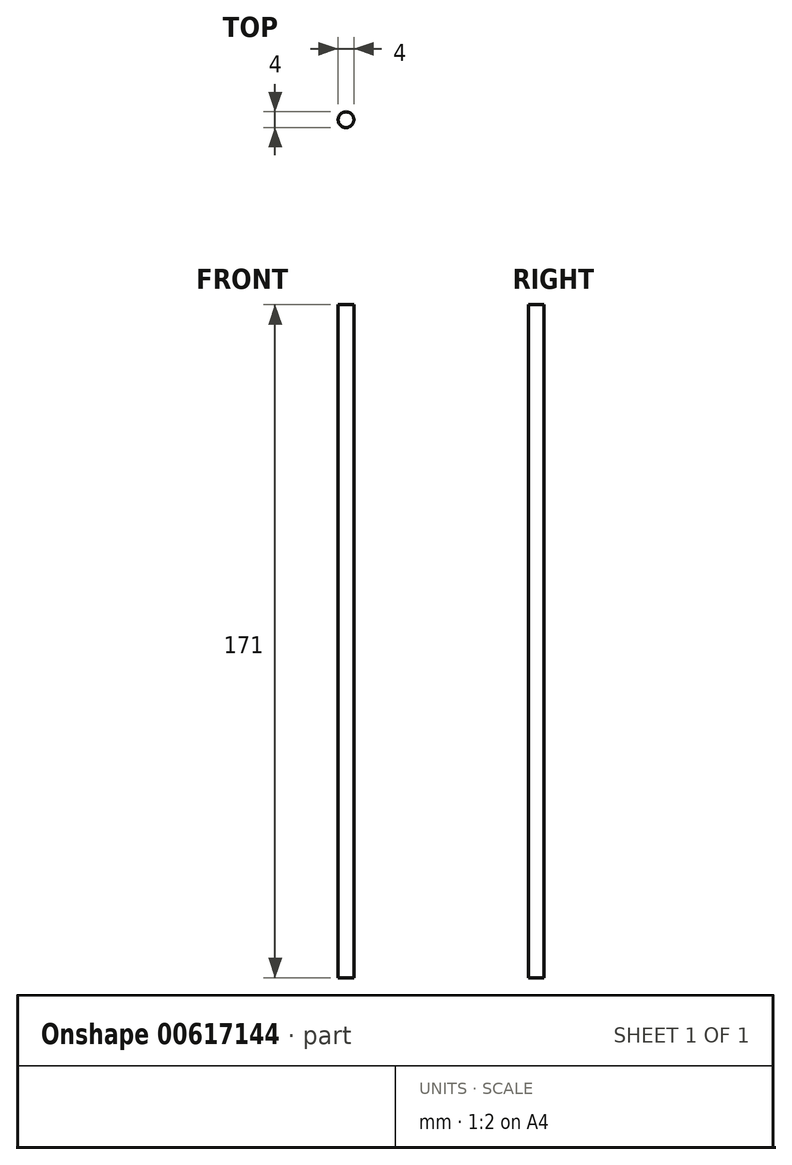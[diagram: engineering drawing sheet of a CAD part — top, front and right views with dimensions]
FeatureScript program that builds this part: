
annotation { "Feature Type Name" : "Feature", "Feature Type Description" : "" }
export const myFeature = defineFeature(function(context is Context, id is Id, definition is map)
    precondition{}
    {
        {
            var Q0;
            Q0=qCreatedBy(makeId("Top.planeOp"),FACE);
            var sketch = newSketch(context, id + "F0", { "sketchPlane" : qUnion([Q0])});
            skCircle(sketch, "E0", {"center": v(0, 0) * mm, "radius": 2 * mm});
            skSolve(sketch);
        }
        {
            var Q0;
            Q0 = qSketchRegion(id + "F0", true);
            extrude(context, id + "F1", {"entities" : qUnion([Q0]), "depth" : 171 * mm, "offsetDistance" : 25 * mm});
        }
    });
